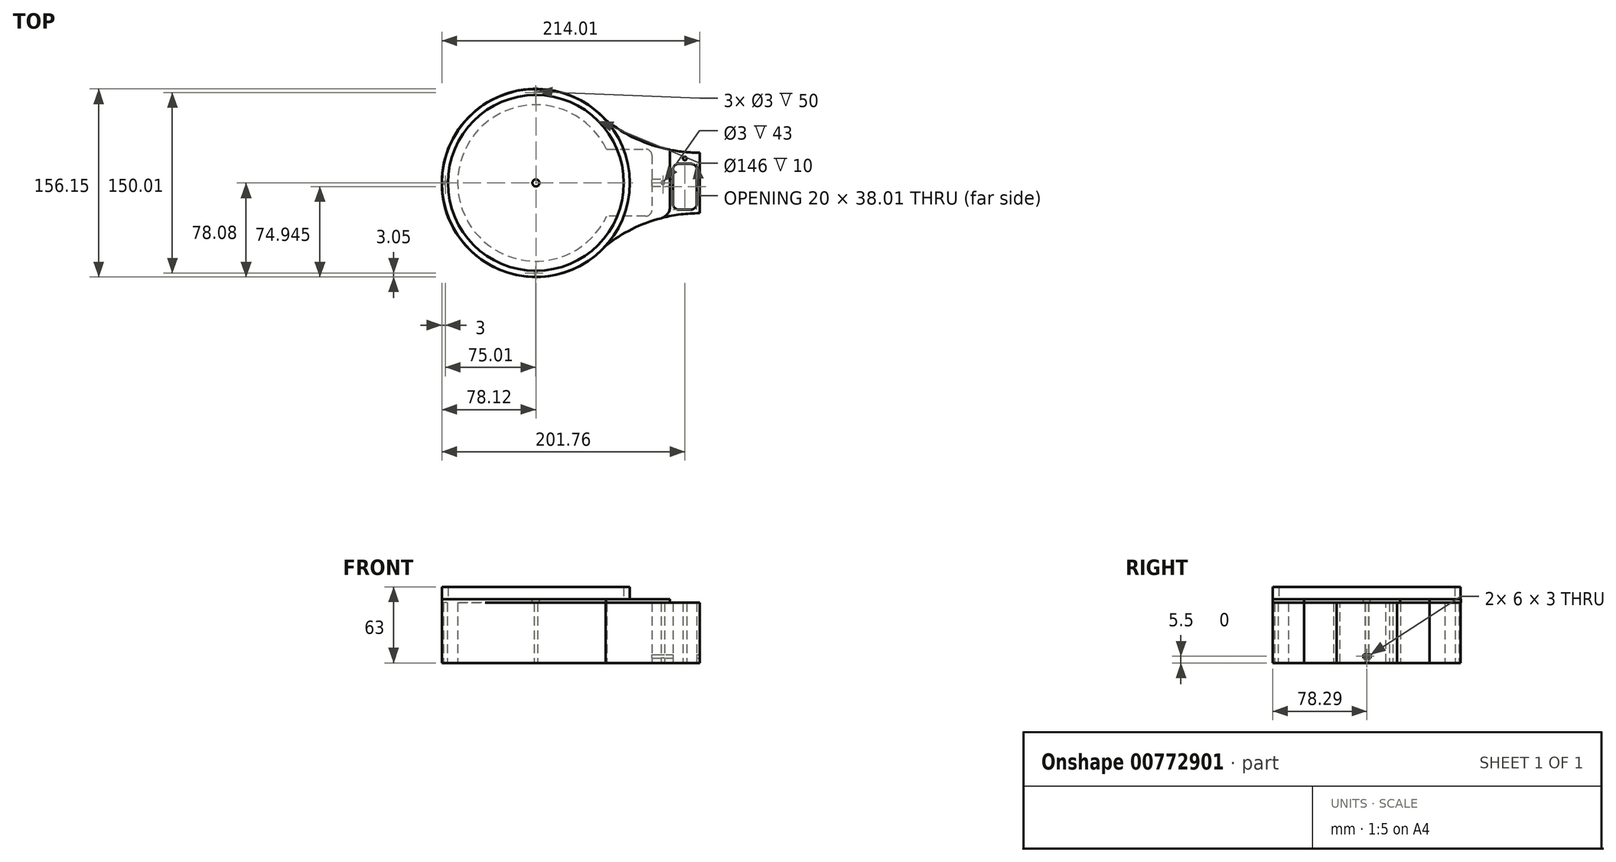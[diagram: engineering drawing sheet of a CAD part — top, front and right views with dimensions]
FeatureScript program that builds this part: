
annotation { "Feature Type Name" : "Feature", "Feature Type Description" : "" }
export const myFeature = defineFeature(function(context is Context, id is Id, definition is map)
    precondition{}
    {
        {
            var Q0;
            Q0=qCreatedBy(makeId("Top.planeOp"),FACE);
            var sketch = newSketch(context, id + "F0", { "sketchPlane" : qUnion([Q0])});
            skArc(sketch, "E0.1", {"start": v(-30.78, 51.78) * mm, "mid": v(-166.92, -0.23) * mm, "end": v(-30.8, -52.26) * mm});
            skLineSegment(sketch, "E0.3", {"start": v(47.1, 18.8) * mm, "end": v(47.08, -19.3) * mm});
            skLineSegment(sketch, "E1", {"start": v(47.09, -0.25) * mm, "end": v(47.09, 24.86) * mm});
            skLineSegment(sketch, "E2", {"start": v(47.09, 24.86) * mm, "end": v(47.09, -25.35) * mm});
            skLineSegment(sketch, "E3", {"start": v(47.09, -25.35) * mm, "end": v(22.59, -25.33) * mm});
            skLineSegment(sketch, "E4", {"start": v(22.59, -25.33) * mm, "end": v(22.59, 24.86) * mm});
            skLineSegment(sketch, "E5", {"start": v(22.59, 24.86) * mm, "end": v(47.09, 24.86) * mm});
            skArc(sketch, "E6", {"start": v(-30.78, 51.78) * mm, "mid": v(5.9, 31.78) * mm, "end": v(47.09, 24.86) * mm});
            skArc(sketch, "E7", {"start": v(47.09, -25.35) * mm, "mid": v(5.89, -32.25) * mm, "end": v(-30.8, -52.26) * mm});
            skLineSegment(sketch, "E8", {"start": v(34.84, -22.35) * mm, "end": v(44.84, -22.35) * mm});
            skLineSegment(sketch, "E9", {"start": v(44.84, -22.35) * mm, "end": v(24.84, -22.34) * mm});
            skLineSegment(sketch, "E10", {"start": v(24.84, -22.34) * mm, "end": v(24.84, 15.66) * mm});
            skLineSegment(sketch, "E11", {"start": v(24.84, 15.66) * mm, "end": v(44.84, 15.65) * mm});
            skLineSegment(sketch, "E12", {"start": v(44.84, 15.65) * mm, "end": v(44.84, -22.35) * mm});
            skCircle(sketch, "E13", {"center": v(16.62, 0) * mm, "radius": 1.5 * mm});
            skCircle(sketch, "E14", {"center": v(34.84, 20.04) * mm, "radius": 1.5 * mm});
            skPoint(sketch, "E14.centerSnap0", {"position": v(34.84, 24.86) * mm});
            skPoint(sketch, "E15.startSnap0", {"position": v(-166.92, -0.23) * mm});
            skCircle(sketch, "E16", {"center": v(-163.92, -0.24) * mm, "radius": 1.5 * mm});
            skCircle(sketch, "E17", {"center": v(-88.91, -75.24) * mm, "radius": 1.5 * mm});
            skCircle(sketch, "E18", {"center": v(-88.91, 74.77) * mm, "radius": 1.5 * mm});
            skSolve(sketch);
        }
        {
            var Q0;
            Q0=makeQuery(id+"F0.imprint","IMPRINT",FACE,{"disambiguationData":[TD([[makeQuery(id+"F0.imprint","IMPRINT",EDGE,{"derivedFrom":sQuery(id+"F0.wireOp",EDGE,"E0.1")}),1.0]])]});
            var sketch = newSketch(context, id + "F1", { "sketchPlane" : qUnion([Q0])});
            skLineSegment(sketch, "E19", {"start": v(22.6, 24.87) * mm, "end": v(22.6, -24.87) * mm});
            skLineSegment(sketch, "E20.left", {"start": v(7.47, 27.76) * mm, "end": v(7.47, -27.78) * mm});
            skLineSegment(sketch, "E21", {"start": v(-30.26, 27.76) * mm, "end": v(7.47, 27.76) * mm});
            skLineSegment(sketch, "E22", {"start": v(7.47, -27.78) * mm, "end": v(-30.05, -27.78) * mm});
            skArc(sketch, "E23", {"start": v(-30.26, 27.76) * mm, "mid": v(-153.75, -0.46) * mm, "end": v(-30.05, -27.78) * mm});
            skSolve(sketch);
        }
        {
            var Q0;
            {var subQ1=sQuery(id+"F0.wireOp",EDGE,"E3");Q0=makeQuery(id+"F0.imprint","IMPRINT",FACE,{"disambiguationData":[TD([[makeQuery(id+"F0.imprint","IMPRINT",EDGE,{"derivedFrom":subQ1}),-1.0]])]});}
            var Q1;
            Q1=makeQuery(id+"F1.imprint","IMPRINT",FACE,{"disambiguationData":[TD([[makeQuery(id+"F1.imprint","IMPRINT",EDGE,{"derivedFrom":sQuery(id+"F1.wireOp",EDGE,"E20.left")}),1.0]])]});
            extrude(context, id + "F2", {"entities" : qUnion([Q0, Q1]), "depth" : 50 * mm, "offsetDistance" : 25 * mm});
        }
        {
            var Q0;
            Q0=makeQuery(id+"F2.opExtrude","SWEPT_EDGE",EDGE,{"disambiguationData":[OSD([sQuery(id+"F1.wireOp",EDGE,"E20.left"),sQuery(id+"F1.wireOp",EDGE,"E21")])]});
            var Q1;
            Q1=makeQuery(id+"F2.opExtrude","SWEPT_EDGE",EDGE,{"disambiguationData":[OSD([sQuery(id+"F1.wireOp",EDGE,"E20.left"),sQuery(id+"F1.wireOp",EDGE,"E22")])]});
            fillet(context, id + "F3", {"entities" : qUnion([Q0, Q1]), "radius" : 5 * mm, "tangentPropagation" : true, "allowEdgeOverflow" : false});
        }
        {
            var Q0;
            Q0=makeQuery(id+"F2.opExtrude","SWEPT_EDGE",EDGE,{"disambiguationData":[OSD([sQuery(id+"F0.wireOp",EDGE,"E11"),sQuery(id+"F0.wireOp",EDGE,"E12")])]});
            var Q1;
            Q1=makeQuery(id+"F2.opExtrude","SWEPT_EDGE",EDGE,{"disambiguationData":[OSD([sQuery(id+"F0.wireOp",EDGE,"E10"),sQuery(id+"F0.wireOp",EDGE,"E11")])]});
            var Q2;
            Q2=makeQuery(id+"F2.opExtrude","SWEPT_EDGE",EDGE,{"disambiguationData":[OSD([sQuery(id+"F0.wireOp",EDGE,"E9"),sQuery(id+"F0.wireOp",EDGE,"E12")])]});
            var Q3;
            Q3=makeQuery(id+"F2.opExtrude","SWEPT_EDGE",EDGE,{"disambiguationData":[OSD([sQuery(id+"F0.wireOp",EDGE,"E9"),sQuery(id+"F0.wireOp",EDGE,"E10")])]});
            fillet(context, id + "F4", {"entities" : qUnion([Q0, Q1, Q2, Q3]), "radius" : 5 * mm, "tangentPropagation" : true, "allowEdgeOverflow" : false});
        }
        {
            var Q0;
            Q0=makeQuery(id+"F2.opExtrude","SWEPT_FACE",FACE,{"disambiguationData":[OSD([sQuery(id+"F0.wireOp",EDGE,"E2")])]});
            var sketch = newSketch(context, id + "F5", { "sketchPlane" : qUnion([Q0])});
            skLineSegment(sketch, "E24", {"start": v(0, 4) * mm, "end": v(3, 4) * mm});
            skLineSegment(sketch, "E25", {"start": v(3, 4) * mm, "end": v(-3, 4) * mm});
            skLineSegment(sketch, "E26", {"start": v(-3, 4) * mm, "end": v(-3, 7) * mm});
            skLineSegment(sketch, "E27", {"start": v(-3, 7) * mm, "end": v(3, 7) * mm});
            skLineSegment(sketch, "E28", {"start": v(3, 7) * mm, "end": v(3, 4) * mm});
            skSolve(sketch);
        }
        {
            var Q0;
            {var subQ0=sQuery(id+"F5.wireOp",EDGE,"E26");Q0=makeQuery(id+"F5.imprint","IMPRINT",FACE,{"disambiguationData":[TD([[makeQuery(id+"F5.imprint","IMPRINT",EDGE,{"derivedFrom":subQ0}),-1.0]])]});}
            extrude(context, id + "F6", {"entities" : qUnion([Q0]), "operationType" : NewBodyOperationType.REMOVE, "oppositeDirection" : true, "depth" : 49 * mm, "offsetDistance" : 25 * mm});
        }
        {
            var Q0;
            Q0=makeQuery(id+"F2.opExtrude","CAP_FACE",FACE,{"disambiguationData":[OSD([sQuery(id+"F0.wireOp",EDGE,"E0.1"),sQuery(id+"F0.wireOp",EDGE,"E3"),sQuery(id+"F0.wireOp",EDGE,"E4"),sQuery(id+"F0.wireOp",EDGE,"E5"),sQuery(id+"F0.wireOp",EDGE,"E6"),sQuery(id+"F0.wireOp",EDGE,"E7"),sQuery(id+"F1.wireOp",EDGE,"E20.left"),sQuery(id+"F1.wireOp",EDGE,"E21"),sQuery(id+"F1.wireOp",EDGE,"E22"),sQuery(id+"F1.wireOp",EDGE,"E23")])],"isStart":false});
            cPlane(context, id + "F7", {"entities" : qUnion([Q0]), "cplaneType" : CPlaneType.OFFSET, "offset" : 0 * mm, "width" : 150 * mm, "height" : 150 * mm});
        }
        {
            var Q0;
            Q0=qCreatedBy(id+"F7.planeOp",FACE);
            var sketch = newSketch(context, id + "F8", { "sketchPlane" : qUnion([Q0])});
            skPoint(sketch, "E29", {"position": v(-88.85, -0.21) * mm});
            skLineSegment(sketch, "E30", {"start": v(22.59, 24.9) * mm, "end": v(22.59, 27.37) * mm});
            skLineSegment(sketch, "E31", {"start": v(22.59, -25.32) * mm, "end": v(22.59, -27.83) * mm});
            skPoint(sketch, "E32", {"position": v(-30.7, 51.93) * mm});
            skPoint(sketch, "E33", {"position": v(-30.68, -52.34) * mm});
            skArc(sketch, "E34", {"start": v(-30.7, 51.93) * mm, "mid": v(-5.52, 36.46) * mm, "end": v(22.59, 27.37) * mm});
            skArc(sketch, "E35", {"start": v(22.59, -27.83) * mm, "mid": v(-5.52, -36.88) * mm, "end": v(-30.68, -52.34) * mm});
            skArc(sketch, "E36", {"start": v(-30.7, 51.93) * mm, "mid": v(-166.88, -0.22) * mm, "end": v(-30.68, -52.34) * mm});
            skLineSegment(sketch, "E37", {"start": v(22.59, 24.9) * mm, "end": v(22.59, -25.32) * mm});
            skSolve(sketch);
        }
        {
            var Q0;
            Q0=makeQuery(id+"F8.imprint","IMPRINT",FACE,{"disambiguationData":[TD([[makeQuery(id+"F8.imprint","IMPRINT",EDGE,{"derivedFrom":sQuery(id+"F8.wireOp",EDGE,"E30")}),1.0]])]});
            extrude(context, id + "F9", {"entities" : qUnion([Q0]), "operationType" : NewBodyOperationType.ADD, "depth" : 3 * mm, "offsetDistance" : 25 * mm});
        }
        {
            var Q0;
            {var subQ2=sQuery(id+"F0.wireOp",EDGE,"E7");var subQ3=sQuery(id+"F0.wireOp",EDGE,"E4");var subQ4=sQuery(id+"F0.wireOp",EDGE,"E3");Q0=makeQuery(id+"F9.boolean.opBoolean","SPLIT",FACE,{"disambiguationData":[TD([makeQuery(id+"F2.opExtrude","SWEPT_FACE",FACE,{"disambiguationData":[OSD([subQ2])]})])],"derivedFrom":makeQuery(id+"F2.opExtrude","CAP_FACE",FACE,{"disambiguationData":[OSD([sQuery(id+"F0.wireOp",EDGE,"E0.1"),subQ4,subQ3,sQuery(id+"F0.wireOp",EDGE,"E5"),sQuery(id+"F0.wireOp",EDGE,"E6"),subQ2,sQuery(id+"F0.wireOp",EDGE,"E13"),sQuery(id+"F0.wireOp",EDGE,"E16"),sQuery(id+"F0.wireOp",EDGE,"E17"),sQuery(id+"F0.wireOp",EDGE,"E18"),sQuery(id+"F1.wireOp",EDGE,"E20.left"),sQuery(id+"F1.wireOp",EDGE,"E21"),sQuery(id+"F1.wireOp",EDGE,"E22"),sQuery(id+"F1.wireOp",EDGE,"E23")])],"isStart":false})});}
            var Q1;
            {var subQ1=sQuery(id+"F0.wireOp",EDGE,"E6");var subQ2=sQuery(id+"F0.wireOp",EDGE,"E5");var subQ3=sQuery(id+"F0.wireOp",EDGE,"E4");Q1=makeQuery(id+"F9.boolean.opBoolean","SPLIT",FACE,{"disambiguationData":[TD([makeQuery(id+"F2.opExtrude","SWEPT_FACE",FACE,{"disambiguationData":[OSD([subQ1])]})])],"derivedFrom":makeQuery(id+"F2.opExtrude","CAP_FACE",FACE,{"disambiguationData":[OSD([sQuery(id+"F0.wireOp",EDGE,"E0.1"),sQuery(id+"F0.wireOp",EDGE,"E3"),subQ3,subQ2,subQ1,sQuery(id+"F0.wireOp",EDGE,"E7"),sQuery(id+"F0.wireOp",EDGE,"E13"),sQuery(id+"F0.wireOp",EDGE,"E16"),sQuery(id+"F0.wireOp",EDGE,"E17"),sQuery(id+"F0.wireOp",EDGE,"E18"),sQuery(id+"F1.wireOp",EDGE,"E20.left"),sQuery(id+"F1.wireOp",EDGE,"E21"),sQuery(id+"F1.wireOp",EDGE,"E22"),sQuery(id+"F1.wireOp",EDGE,"E23")])],"isStart":false})});}
            extrude(context, id + "F10", {"entities" : qUnion([Q0, Q1]), "operationType" : NewBodyOperationType.ADD, "depth" : 3 * mm, "offsetDistance" : 25 * mm});
        }
        {
            var Q0;
            Q0=makeQuery(id+"F10.opExtrude","SWEPT_EDGE",EDGE,{"disambiguationData":[OSD([sQuery(id+"F0.wireOp",EDGE,"E4"),sQuery(id+"F0.wireOp",EDGE,"E5")])]});
            var Q1;
            {var subQ0=sQuery(id+"F8.wireOp",EDGE,"E37");var subQ1=sQuery(id+"F8.wireOp",EDGE,"E31");Q1=makeQuery(id+"F10.boolean.opBoolean","MERGE",EDGE,{"derivedFrom":[makeQuery(id+"F9.opExtrude","SWEPT_EDGE",EDGE,{"disambiguationData":[OSD([subQ1,subQ0])]}),makeQuery(id+"F10.opExtrude","SWEPT_EDGE",EDGE,{"disambiguationData":[OSD([sQuery(id+"F0.wireOp",EDGE,"E3"),sQuery(id+"F0.wireOp",EDGE,"E4"),subQ1,subQ0])]})]});}
            fillet(context, id + "F11", {"entities" : qUnion([Q0, Q1]), "radius" : 10 * mm, "tangentPropagation" : true, "allowEdgeOverflow" : false});
        }
        {
            var Q0;
            {var subQ0=sQuery(id+"F8.wireOp",EDGE,"E30");var subQ1=sQuery(id+"F0.wireOp",EDGE,"E6");var subQ2=sQuery(id+"F0.wireOp",EDGE,"E5");var subQ3=sQuery(id+"F0.wireOp",EDGE,"E4");var subQ5=sQuery(id+"F8.wireOp",EDGE,"E37");var subQ6=sQuery(id+"F8.wireOp",EDGE,"E36");var subQ7=sQuery(id+"F8.wireOp",EDGE,"E35");var subQ8=sQuery(id+"F8.wireOp",EDGE,"E34");var subQ9=sQuery(id+"F8.wireOp",EDGE,"E31");var subQ12=sQuery(id+"F1.wireOp",EDGE,"E23");var subQ13=sQuery(id+"F1.wireOp",EDGE,"E22");var subQ14=sQuery(id+"F1.wireOp",EDGE,"E21");var subQ15=sQuery(id+"F1.wireOp",EDGE,"E20.left");var subQ16=sQuery(id+"F0.wireOp",EDGE,"E18");var subQ17=sQuery(id+"F0.wireOp",EDGE,"E17");var subQ18=sQuery(id+"F0.wireOp",EDGE,"E16");var subQ19=sQuery(id+"F0.wireOp",EDGE,"E13");var subQ20=sQuery(id+"F0.wireOp",EDGE,"E7");var subQ21=sQuery(id+"F0.wireOp",EDGE,"E3");var subQ22=sQuery(id+"F0.wireOp",EDGE,"E0.1");var subQ23=makeQuery(id+"F2.opExtrude","CAP_FACE",FACE,{"disambiguationData":[OSD([subQ22,subQ21,subQ3,subQ2,subQ1,subQ20,subQ19,subQ18,subQ17,subQ16,subQ15,subQ14,subQ13,subQ12])],"isStart":false});Q0=makeQuery(id+"F10.boolean.opBoolean","MERGE",FACE,{"derivedFrom":[makeQuery(id+"F9.opExtrude","CAP_FACE",FACE,{"disambiguationData":[OSD([subQ0,subQ9,subQ8,subQ7,subQ6,subQ5])],"isStart":false}),makeQuery(id+"F10.opExtrude","CAP_FACE",FACE,{"disambiguationData":[OSD([subQ22,subQ21,subQ3,subQ2,subQ1,subQ20,subQ19,subQ18,subQ17,subQ16,subQ15,subQ14,subQ13,subQ12]),TDD([makeQuery(id+"F9.boolean.opBoolean","SPLIT",FACE,{"disambiguationData":[TD([makeQuery(id+"F2.opExtrude","SWEPT_FACE",FACE,{"disambiguationData":[OSD([subQ20])]})])],"derivedFrom":subQ23})])],"isStart":false}),makeQuery(id+"F10.opExtrude","CAP_FACE",FACE,{"disambiguationData":[OSD([subQ22,subQ21,subQ3,subQ2,subQ1,subQ20,subQ19,subQ18,subQ17,subQ16,subQ15,subQ14,subQ13,subQ12]),TDD([makeQuery(id+"F9.boolean.opBoolean","SPLIT",FACE,{"disambiguationData":[TD([makeQuery(id+"F2.opExtrude","SWEPT_FACE",FACE,{"disambiguationData":[OSD([subQ1])]})])],"derivedFrom":subQ23})])],"isStart":false})]});}
            var sketch = newSketch(context, id + "F12", { "sketchPlane" : qUnion([Q0])});
            skCircle(sketch, "E38", {"center": v(-88.8, -0.21) * mm, "radius": 73 * mm});
            skCircle(sketch, "E39", {"center": v(-88.8, -0.21) * mm, "radius": 78 * mm});
            skSolve(sketch);
        }
        {
            var Q0;
            Q0=makeQuery(id+"F12.imprint","IMPRINT",FACE,{"disambiguationData":[TD([[makeQuery(id+"F12.imprint","IMPRINT",EDGE,{"derivedFrom":sQuery(id+"F12.wireOp",EDGE,"E38")}),-1.0]])]});
            extrude(context, id + "F13", {"entities" : qUnion([Q0]), "operationType" : NewBodyOperationType.ADD, "depth" : 10 * mm, "offsetDistance" : 25 * mm});
        }
        {
            var Q0;
            {var subQ0=sQuery(id+"F8.wireOp",EDGE,"E30");var subQ1=sQuery(id+"F0.wireOp",EDGE,"E6");var subQ2=sQuery(id+"F0.wireOp",EDGE,"E5");var subQ3=sQuery(id+"F0.wireOp",EDGE,"E4");var subQ5=sQuery(id+"F8.wireOp",EDGE,"E37");var subQ6=sQuery(id+"F8.wireOp",EDGE,"E36");var subQ7=sQuery(id+"F8.wireOp",EDGE,"E35");var subQ8=sQuery(id+"F8.wireOp",EDGE,"E34");var subQ9=sQuery(id+"F8.wireOp",EDGE,"E31");var subQ12=sQuery(id+"F1.wireOp",EDGE,"E23");var subQ13=sQuery(id+"F1.wireOp",EDGE,"E22");var subQ14=sQuery(id+"F1.wireOp",EDGE,"E21");var subQ15=sQuery(id+"F1.wireOp",EDGE,"E20.left");var subQ16=sQuery(id+"F0.wireOp",EDGE,"E18");var subQ17=sQuery(id+"F0.wireOp",EDGE,"E17");var subQ18=sQuery(id+"F0.wireOp",EDGE,"E16");var subQ19=sQuery(id+"F0.wireOp",EDGE,"E13");var subQ20=sQuery(id+"F0.wireOp",EDGE,"E7");var subQ21=sQuery(id+"F0.wireOp",EDGE,"E3");var subQ22=sQuery(id+"F0.wireOp",EDGE,"E0.1");var subQ23=makeQuery(id+"F2.opExtrude","CAP_FACE",FACE,{"disambiguationData":[OSD([subQ22,subQ21,subQ3,subQ2,subQ1,subQ20,subQ19,subQ18,subQ17,subQ16,subQ15,subQ14,subQ13,subQ12])],"isStart":false});Q0=makeQuery(id+"F13.boolean.opBoolean","SPLIT",FACE,{"disambiguationData":[TD([makeQuery(id+"F13.opExtrude","SWEPT_FACE",FACE,{"disambiguationData":[OSD([sQuery(id+"F12.wireOp",EDGE,"E38")])]})])],"derivedFrom":makeQuery(id+"F10.boolean.opBoolean","MERGE",FACE,{"derivedFrom":[makeQuery(id+"F9.opExtrude","CAP_FACE",FACE,{"disambiguationData":[OSD([subQ0,subQ9,subQ8,subQ7,subQ6,subQ5])],"isStart":false}),makeQuery(id+"F10.opExtrude","CAP_FACE",FACE,{"disambiguationData":[OSD([subQ22,subQ21,subQ3,subQ2,subQ1,subQ20,subQ19,subQ18,subQ17,subQ16,subQ15,subQ14,subQ13,subQ12]),TDD([makeQuery(id+"F9.boolean.opBoolean","SPLIT",FACE,{"disambiguationData":[TD([makeQuery(id+"F2.opExtrude","SWEPT_FACE",FACE,{"disambiguationData":[OSD([subQ20])]})])],"derivedFrom":subQ23})])],"isStart":false}),makeQuery(id+"F10.opExtrude","CAP_FACE",FACE,{"disambiguationData":[OSD([subQ22,subQ21,subQ3,subQ2,subQ1,subQ20,subQ19,subQ18,subQ17,subQ16,subQ15,subQ14,subQ13,subQ12]),TDD([makeQuery(id+"F9.boolean.opBoolean","SPLIT",FACE,{"disambiguationData":[TD([makeQuery(id+"F2.opExtrude","SWEPT_FACE",FACE,{"disambiguationData":[OSD([subQ1])]})])],"derivedFrom":subQ23})])],"isStart":false})]})});}
            var sketch = newSketch(context, id + "F14", { "sketchPlane" : qUnion([Q0])});
            skCircle(sketch, "E40", {"center": v(-88.8, -0.21) * mm, "radius": 2.9 * mm});
            skSolve(sketch);
        }
        {
            var Q0;
            Q0=makeQuery(id+"F14.imprint","IMPRINT",FACE,{"disambiguationData":[TD([[makeQuery(id+"F14.imprint","IMPRINT",EDGE,{"derivedFrom":sQuery(id+"F14.wireOp",EDGE,"E40")}),1.0]])]});
            extrude(context, id + "F15", {"entities" : qUnion([Q0]), "operationType" : NewBodyOperationType.REMOVE, "oppositeDirection" : true, "depth" : 8 * mm, "offsetDistance" : 25 * mm});
        }
    });
